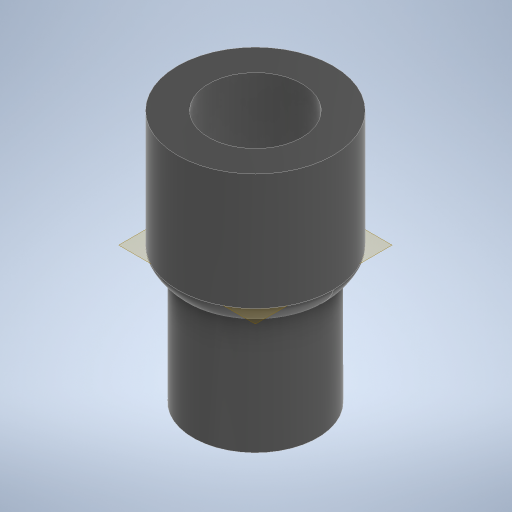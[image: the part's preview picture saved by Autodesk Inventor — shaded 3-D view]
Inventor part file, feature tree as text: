
AUTODESK INVENTOR PART (.ipt)
format: ipt  version: 2024 (Build 280153000, 153)  size: 303,616 bytes
history: native  units: mm
features: other x3, extrude x2, sketch x2, plane x1, loft x1
ambient origin geometry x8: Origin, YZ Plane, XZ Plane, XY Plane, X Axis, Y Axis, Z Axis, Center Point
bodies: Solid1 (feature_tree)
feature tree (9):
  extrude  "Extrusion1"  Depth=10.0mm
  plane  "Work Plane1"
  extrude  "Extrusion2"  Depth=2.5mm
  loft  "Loft1"
  sketch  "Sketch1"  dims[d0=16.0mm d1=10.0mm]
  sketch  "Sketch2"  dims[d2=15.0mm d3=0.0mm d4=2.5mm d5=20.0mm d6=12.0mm d7=15.0mm d8=0.0mm d9=0.0mm d10=90.0deg d11=0.0mm d12=90.0deg d13=0.0mm d14=90.0deg]
  other  "Edges1"
  other  "Edges2"
  other  "Edges3"
